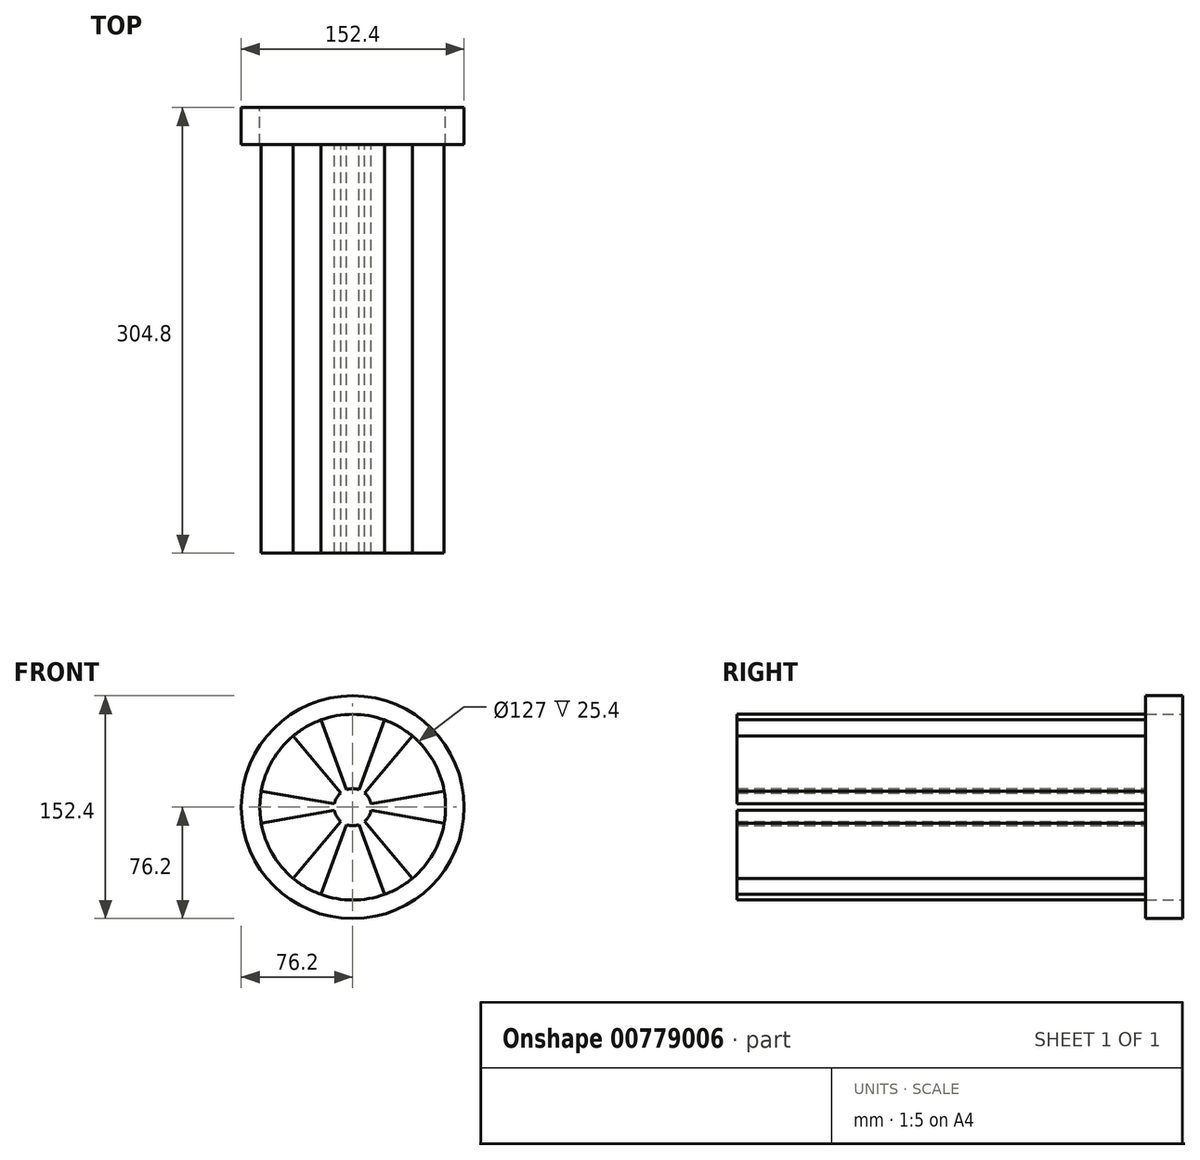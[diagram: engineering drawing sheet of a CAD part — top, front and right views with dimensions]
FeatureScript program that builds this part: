
annotation { "Feature Type Name" : "Feature", "Feature Type Description" : "" }
export const myFeature = defineFeature(function(context is Context, id is Id, definition is map)
    precondition{}
    {
        {
            var Q0;
            Q0=qCreatedBy(makeId("Front.planeOp"),FACE);
            var sketch = newSketch(context, id + "F0", { "sketchPlane" : qUnion([Q0])});
            skCircle(sketch, "E0", {"center": v(0, 0) * mm, "radius": 76.2 * mm});
            skCircle(sketch, "E1", {"center": v(0, 0) * mm, "radius": 12.7 * mm});
            skLineSegment(sketch, "E2", {"start": v(0, 12.7) * mm, "end": v(0, 76.2) * mm});
            skLineSegment(sketch, "E3.1.0", {"start": v(-4.34, 11.93) * mm, "end": v(-26.06, 71.6) * mm});
            skLineSegment(sketch, "E3.2.0", {"start": v(-8.16, 9.73) * mm, "end": v(-48.98, 58.37) * mm});
            skLineSegment(sketch, "E3.3.0", {"start": v(-11, 6.35) * mm, "end": v(-66, 38.1) * mm});
            skLineSegment(sketch, "E3.4.0", {"start": v(-12.5, 2.2) * mm, "end": v(-75.04, 13.23) * mm});
            skLineSegment(sketch, "E3.5.0", {"start": v(-12.5, -2.2) * mm, "end": v(-75.04, -13.23) * mm});
            skLineSegment(sketch, "E3.6.0", {"start": v(-11, -6.35) * mm, "end": v(-66, -38.1) * mm});
            skLineSegment(sketch, "E3.7.0", {"start": v(-8.16, -9.73) * mm, "end": v(-48.98, -58.37) * mm});
            skLineSegment(sketch, "E3.8.0", {"start": v(-4.34, -11.93) * mm, "end": v(-26.06, -71.6) * mm});
            skLineSegment(sketch, "E3.9.0", {"start": v(0, -12.7) * mm, "end": v(0, -76.2) * mm});
            skLineSegment(sketch, "E3.10.0", {"start": v(4.34, -11.93) * mm, "end": v(26.06, -71.6) * mm});
            skLineSegment(sketch, "E3.11.0", {"start": v(8.16, -9.73) * mm, "end": v(48.98, -58.37) * mm});
            skLineSegment(sketch, "E3.12.0", {"start": v(11, -6.35) * mm, "end": v(66, -38.1) * mm});
            skLineSegment(sketch, "E3.13.0", {"start": v(12.5, -2.2) * mm, "end": v(75.04, -13.23) * mm});
            skLineSegment(sketch, "E3.14.0", {"start": v(12.5, 2.2) * mm, "end": v(75.04, 13.23) * mm});
            skLineSegment(sketch, "E3.15.0", {"start": v(11, 6.35) * mm, "end": v(66, 38.1) * mm});
            skLineSegment(sketch, "E3.16.0", {"start": v(8.16, 9.73) * mm, "end": v(48.98, 58.37) * mm});
            skLineSegment(sketch, "E3.17.0", {"start": v(4.34, 11.93) * mm, "end": v(26.06, 71.6) * mm});
            skCircle(sketch, "E4", {"center": v(0, 0) * mm, "radius": 63.5 * mm});
            skSolve(sketch);
        }
        {
            var Q0;
            {var subQ0=sQuery(id+"F0.wireOp",EDGE,"E1");var subQ8=makeQuery(id+"F0.imprint","INTERSECT",VERTEX,{"derivedFrom":[subQ0,sQuery(id+"F0.wireOp",EDGE,"E3.14.0")]});Q0=makeQuery(id+"F0.imprint","IMPRINT",FACE,{"disambiguationData":[TD([[makeQuery(id+"F0.imprint","IMPRINT",EDGE,{"disambiguationData":[TD([[subQ8,-1.0]])],"derivedFrom":subQ0}),1.0]])]});}
            var Q1;
            {var subQ0=sQuery(id+"F0.wireOp",EDGE,"E3.5.0");var subQ1=sQuery(id+"F0.wireOp",EDGE,"E1");var subQ2=makeQuery(id+"F0.imprint","INTERSECT",VERTEX,{"derivedFrom":[subQ1,subQ0]});Q1=makeQuery(id+"F0.imprint","IMPRINT",FACE,{"disambiguationData":[TD([[makeQuery(id+"F0.imprint","IMPRINT",EDGE,{"disambiguationData":[TD([[subQ2,-1.0]])],"derivedFrom":subQ1}),-1.0]])]});}
            var Q2;
            {var subQ0=sQuery(id+"F0.wireOp",EDGE,"E2");var subQ1=sQuery(id+"F0.wireOp",EDGE,"E1");var subQ2=makeQuery(id+"F0.imprint","INTERSECT",VERTEX,{"derivedFrom":[subQ1,subQ0]});Q2=makeQuery(id+"F0.imprint","IMPRINT",FACE,{"disambiguationData":[TD([[makeQuery(id+"F0.imprint","IMPRINT",EDGE,{"disambiguationData":[TD([[subQ2,1.0]])],"derivedFrom":subQ1}),-1.0]])]});}
            var Q3;
            {var subQ0=sQuery(id+"F0.wireOp",EDGE,"E3.2.0");var subQ1=sQuery(id+"F0.wireOp",EDGE,"E1");var subQ2=makeQuery(id+"F0.imprint","INTERSECT",VERTEX,{"derivedFrom":[subQ1,subQ0]});Q3=makeQuery(id+"F0.imprint","IMPRINT",FACE,{"disambiguationData":[TD([[makeQuery(id+"F0.imprint","IMPRINT",EDGE,{"disambiguationData":[TD([[subQ2,-1.0]])],"derivedFrom":subQ1}),-1.0]])]});}
            var Q4;
            {var subQ0=sQuery(id+"F0.wireOp",EDGE,"E3.11.0");var subQ1=sQuery(id+"F0.wireOp",EDGE,"E1");var subQ2=makeQuery(id+"F0.imprint","INTERSECT",VERTEX,{"derivedFrom":[subQ1,subQ0]});Q4=makeQuery(id+"F0.imprint","IMPRINT",FACE,{"disambiguationData":[TD([[makeQuery(id+"F0.imprint","IMPRINT",EDGE,{"disambiguationData":[TD([[subQ2,-1.0]])],"derivedFrom":subQ1}),-1.0]])]});}
            var Q5;
            {var subQ0=sQuery(id+"F0.wireOp",EDGE,"E3.14.0");var subQ1=sQuery(id+"F0.wireOp",EDGE,"E1");var subQ2=makeQuery(id+"F0.imprint","INTERSECT",VERTEX,{"derivedFrom":[subQ1,subQ0]});Q5=makeQuery(id+"F0.imprint","IMPRINT",FACE,{"disambiguationData":[TD([[makeQuery(id+"F0.imprint","IMPRINT",EDGE,{"disambiguationData":[TD([[subQ2,-1.0]])],"derivedFrom":subQ1}),-1.0]])]});}
            var Q6;
            {var subQ0=sQuery(id+"F0.wireOp",EDGE,"E3.8.0");var subQ1=sQuery(id+"F0.wireOp",EDGE,"E1");var subQ2=makeQuery(id+"F0.imprint","INTERSECT",VERTEX,{"derivedFrom":[subQ1,subQ0]});Q6=makeQuery(id+"F0.imprint","IMPRINT",FACE,{"disambiguationData":[TD([[makeQuery(id+"F0.imprint","IMPRINT",EDGE,{"disambiguationData":[TD([[subQ2,-1.0]])],"derivedFrom":subQ1}),-1.0]])]});}
            extrude(context, id + "F1", {"entities" : qUnion([Q0, Q1, Q2, Q3, Q4, Q5, Q6]), "depth" : 25.4 * mm, "offsetDistance" : 25.4 * mm});
        }
        {
            var Q0;
            {var subQ0=sQuery(id+"F0.wireOp",EDGE,"E3.9.0");var subQ1=sQuery(id+"F0.wireOp",EDGE,"E0");var subQ2=makeQuery(id+"F0.imprint","INTERSECT",VERTEX,{"derivedFrom":[subQ1,subQ0]});Q0=makeQuery(id+"F0.imprint","IMPRINT",FACE,{"disambiguationData":[TD([[makeQuery(id+"F0.imprint","IMPRINT",EDGE,{"disambiguationData":[TD([[subQ2,-1.0]])],"derivedFrom":subQ1}),1.0]])]});}
            var Q1;
            {var subQ0=sQuery(id+"F0.wireOp",EDGE,"E3.13.0");var subQ1=sQuery(id+"F0.wireOp",EDGE,"E0");var subQ2=makeQuery(id+"F0.imprint","INTERSECT",VERTEX,{"derivedFrom":[subQ1,subQ0]});Q1=makeQuery(id+"F0.imprint","IMPRINT",FACE,{"disambiguationData":[TD([[makeQuery(id+"F0.imprint","IMPRINT",EDGE,{"disambiguationData":[TD([[subQ2,-1.0]])],"derivedFrom":subQ1}),1.0]])]});}
            var Q2;
            {var subQ0=sQuery(id+"F0.wireOp",EDGE,"E2");var subQ1=sQuery(id+"F0.wireOp",EDGE,"E0");var subQ2=makeQuery(id+"F0.imprint","INTERSECT",VERTEX,{"derivedFrom":[subQ1,subQ0]});Q2=makeQuery(id+"F0.imprint","IMPRINT",FACE,{"disambiguationData":[TD([[makeQuery(id+"F0.imprint","IMPRINT",EDGE,{"disambiguationData":[TD([[subQ2,-1.0]])],"derivedFrom":subQ1}),1.0]])]});}
            var Q3;
            {var subQ0=sQuery(id+"F0.wireOp",EDGE,"E3.3.0");var subQ1=sQuery(id+"F0.wireOp",EDGE,"E0");var subQ2=makeQuery(id+"F0.imprint","INTERSECT",VERTEX,{"derivedFrom":[subQ1,subQ0]});Q3=makeQuery(id+"F0.imprint","IMPRINT",FACE,{"disambiguationData":[TD([[makeQuery(id+"F0.imprint","IMPRINT",EDGE,{"disambiguationData":[TD([[subQ2,-1.0]])],"derivedFrom":subQ1}),1.0]])]});}
            var Q4;
            {var subQ0=sQuery(id+"F0.wireOp",EDGE,"E3.5.0");var subQ1=sQuery(id+"F0.wireOp",EDGE,"E0");var subQ2=makeQuery(id+"F0.imprint","INTERSECT",VERTEX,{"derivedFrom":[subQ1,subQ0]});Q4=makeQuery(id+"F0.imprint","IMPRINT",FACE,{"disambiguationData":[TD([[makeQuery(id+"F0.imprint","IMPRINT",EDGE,{"disambiguationData":[TD([[subQ2,-1.0]])],"derivedFrom":subQ1}),1.0]])]});}
            var Q5;
            {var subQ0=sQuery(id+"F0.wireOp",EDGE,"E3.7.0");var subQ1=sQuery(id+"F0.wireOp",EDGE,"E0");var subQ2=makeQuery(id+"F0.imprint","INTERSECT",VERTEX,{"derivedFrom":[subQ1,subQ0]});Q5=makeQuery(id+"F0.imprint","IMPRINT",FACE,{"disambiguationData":[TD([[makeQuery(id+"F0.imprint","IMPRINT",EDGE,{"disambiguationData":[TD([[subQ2,-1.0]])],"derivedFrom":subQ1}),1.0]])]});}
            var Q6;
            {var subQ0=sQuery(id+"F0.wireOp",EDGE,"E2");var subQ1=sQuery(id+"F0.wireOp",EDGE,"E0");var subQ2=makeQuery(id+"F0.imprint","INTERSECT",VERTEX,{"derivedFrom":[subQ1,subQ0]});Q6=makeQuery(id+"F0.imprint","IMPRINT",FACE,{"disambiguationData":[TD([[makeQuery(id+"F0.imprint","IMPRINT",EDGE,{"disambiguationData":[TD([[subQ2,1.0]])],"derivedFrom":subQ1}),1.0]])]});}
            var Q7;
            {var subQ0=sQuery(id+"F0.wireOp",EDGE,"E3.10.0");var subQ1=sQuery(id+"F0.wireOp",EDGE,"E0");var subQ2=makeQuery(id+"F0.imprint","INTERSECT",VERTEX,{"derivedFrom":[subQ1,subQ0]});Q7=makeQuery(id+"F0.imprint","IMPRINT",FACE,{"disambiguationData":[TD([[makeQuery(id+"F0.imprint","IMPRINT",EDGE,{"disambiguationData":[TD([[subQ2,-1.0]])],"derivedFrom":subQ1}),1.0]])]});}
            var Q8;
            {var subQ0=sQuery(id+"F0.wireOp",EDGE,"E3.14.0");var subQ1=sQuery(id+"F0.wireOp",EDGE,"E0");var subQ2=makeQuery(id+"F0.imprint","INTERSECT",VERTEX,{"derivedFrom":[subQ1,subQ0]});Q8=makeQuery(id+"F0.imprint","IMPRINT",FACE,{"disambiguationData":[TD([[makeQuery(id+"F0.imprint","IMPRINT",EDGE,{"disambiguationData":[TD([[subQ2,-1.0]])],"derivedFrom":subQ1}),1.0]])]});}
            var Q9;
            {var subQ0=sQuery(id+"F0.wireOp",EDGE,"E3.11.0");var subQ1=sQuery(id+"F0.wireOp",EDGE,"E0");var subQ2=makeQuery(id+"F0.imprint","INTERSECT",VERTEX,{"derivedFrom":[subQ1,subQ0]});Q9=makeQuery(id+"F0.imprint","IMPRINT",FACE,{"disambiguationData":[TD([[makeQuery(id+"F0.imprint","IMPRINT",EDGE,{"disambiguationData":[TD([[subQ2,-1.0]])],"derivedFrom":subQ1}),1.0]])]});}
            var Q10;
            {var subQ0=sQuery(id+"F0.wireOp",EDGE,"E3.8.0");var subQ1=sQuery(id+"F0.wireOp",EDGE,"E0");var subQ2=makeQuery(id+"F0.imprint","INTERSECT",VERTEX,{"derivedFrom":[subQ1,subQ0]});Q10=makeQuery(id+"F0.imprint","IMPRINT",FACE,{"disambiguationData":[TD([[makeQuery(id+"F0.imprint","IMPRINT",EDGE,{"disambiguationData":[TD([[subQ2,-1.0]])],"derivedFrom":subQ1}),1.0]])]});}
            var Q11;
            {var subQ0=sQuery(id+"F0.wireOp",EDGE,"E3.15.0");var subQ1=sQuery(id+"F0.wireOp",EDGE,"E0");var subQ2=makeQuery(id+"F0.imprint","INTERSECT",VERTEX,{"derivedFrom":[subQ1,subQ0]});Q11=makeQuery(id+"F0.imprint","IMPRINT",FACE,{"disambiguationData":[TD([[makeQuery(id+"F0.imprint","IMPRINT",EDGE,{"disambiguationData":[TD([[subQ2,-1.0]])],"derivedFrom":subQ1}),1.0]])]});}
            var Q12;
            Q12 = qSketchRegion(id + "F0", true);
            var Q13;
            {var subQ0=sQuery(id+"F0.wireOp",EDGE,"E3.4.0");var subQ1=sQuery(id+"F0.wireOp",EDGE,"E0");var subQ2=makeQuery(id+"F0.imprint","INTERSECT",VERTEX,{"derivedFrom":[subQ1,subQ0]});Q13=makeQuery(id+"F0.imprint","IMPRINT",FACE,{"disambiguationData":[TD([[makeQuery(id+"F0.imprint","IMPRINT",EDGE,{"disambiguationData":[TD([[subQ2,-1.0]])],"derivedFrom":subQ1}),1.0]])]});}
            var Q14;
            {var subQ0=sQuery(id+"F0.wireOp",EDGE,"E3.12.0");var subQ1=sQuery(id+"F0.wireOp",EDGE,"E0");var subQ2=makeQuery(id+"F0.imprint","INTERSECT",VERTEX,{"derivedFrom":[subQ1,subQ0]});Q14=makeQuery(id+"F0.imprint","IMPRINT",FACE,{"disambiguationData":[TD([[makeQuery(id+"F0.imprint","IMPRINT",EDGE,{"disambiguationData":[TD([[subQ2,-1.0]])],"derivedFrom":subQ1}),1.0]])]});}
            var Q15;
            {var subQ0=sQuery(id+"F0.wireOp",EDGE,"E3.2.0");var subQ1=sQuery(id+"F0.wireOp",EDGE,"E0");var subQ2=makeQuery(id+"F0.imprint","INTERSECT",VERTEX,{"derivedFrom":[subQ1,subQ0]});Q15=makeQuery(id+"F0.imprint","IMPRINT",FACE,{"disambiguationData":[TD([[makeQuery(id+"F0.imprint","IMPRINT",EDGE,{"disambiguationData":[TD([[subQ2,-1.0]])],"derivedFrom":subQ1}),1.0]])]});}
            var Q16;
            {var subQ0=sQuery(id+"F0.wireOp",EDGE,"E3.16.0");var subQ1=sQuery(id+"F0.wireOp",EDGE,"E0");var subQ2=makeQuery(id+"F0.imprint","INTERSECT",VERTEX,{"derivedFrom":[subQ1,subQ0]});Q16=makeQuery(id+"F0.imprint","IMPRINT",FACE,{"disambiguationData":[TD([[makeQuery(id+"F0.imprint","IMPRINT",EDGE,{"disambiguationData":[TD([[subQ2,-1.0]])],"derivedFrom":subQ1}),1.0]])]});}
            var Q17;
            {var subQ0=sQuery(id+"F0.wireOp",EDGE,"E3.1.0");var subQ1=sQuery(id+"F0.wireOp",EDGE,"E0");var subQ2=makeQuery(id+"F0.imprint","INTERSECT",VERTEX,{"derivedFrom":[subQ1,subQ0]});Q17=makeQuery(id+"F0.imprint","IMPRINT",FACE,{"disambiguationData":[TD([[makeQuery(id+"F0.imprint","IMPRINT",EDGE,{"disambiguationData":[TD([[subQ2,-1.0]])],"derivedFrom":subQ1}),1.0]])]});}
            var Q18;
            {var subQ0=sQuery(id+"F0.wireOp",EDGE,"E3.6.0");var subQ1=sQuery(id+"F0.wireOp",EDGE,"E0");var subQ2=makeQuery(id+"F0.imprint","INTERSECT",VERTEX,{"derivedFrom":[subQ1,subQ0]});Q18=makeQuery(id+"F0.imprint","IMPRINT",FACE,{"disambiguationData":[TD([[makeQuery(id+"F0.imprint","IMPRINT",EDGE,{"disambiguationData":[TD([[subQ2,-1.0]])],"derivedFrom":subQ1}),1.0]])]});}
            var Q19;
            {var subQ0=sQuery(id+"F0.wireOp",EDGE,"E3.1.0");var subQ1=sQuery(id+"F0.wireOp",EDGE,"E1");var subQ2=makeQuery(id+"F0.imprint","INTERSECT",VERTEX,{"derivedFrom":[subQ1,subQ0]});Q19=makeQuery(id+"F0.imprint","IMPRINT",FACE,{"disambiguationData":[TD([[makeQuery(id+"F0.imprint","IMPRINT",EDGE,{"disambiguationData":[TD([[subQ2,-1.0]])],"derivedFrom":subQ1}),-1.0]])]});}
            var Q20;
            {var subQ0=sQuery(id+"F0.wireOp",EDGE,"E3.16.0");var subQ1=sQuery(id+"F0.wireOp",EDGE,"E1");var subQ2=makeQuery(id+"F0.imprint","INTERSECT",VERTEX,{"derivedFrom":[subQ1,subQ0]});Q20=makeQuery(id+"F0.imprint","IMPRINT",FACE,{"disambiguationData":[TD([[makeQuery(id+"F0.imprint","IMPRINT",EDGE,{"disambiguationData":[TD([[subQ2,-1.0]])],"derivedFrom":subQ1}),-1.0]])]});}
            var Q21;
            {var subQ0=sQuery(id+"F0.wireOp",EDGE,"E3.13.0");var subQ1=sQuery(id+"F0.wireOp",EDGE,"E1");var subQ2=makeQuery(id+"F0.imprint","INTERSECT",VERTEX,{"derivedFrom":[subQ1,subQ0]});Q21=makeQuery(id+"F0.imprint","IMPRINT",FACE,{"disambiguationData":[TD([[makeQuery(id+"F0.imprint","IMPRINT",EDGE,{"disambiguationData":[TD([[subQ2,-1.0]])],"derivedFrom":subQ1}),-1.0]])]});}
            var Q22;
            {var subQ0=sQuery(id+"F0.wireOp",EDGE,"E3.10.0");var subQ1=sQuery(id+"F0.wireOp",EDGE,"E1");var subQ2=makeQuery(id+"F0.imprint","INTERSECT",VERTEX,{"derivedFrom":[subQ1,subQ0]});Q22=makeQuery(id+"F0.imprint","IMPRINT",FACE,{"disambiguationData":[TD([[makeQuery(id+"F0.imprint","IMPRINT",EDGE,{"disambiguationData":[TD([[subQ2,-1.0]])],"derivedFrom":subQ1}),-1.0]])]});}
            var Q23;
            {var subQ0=sQuery(id+"F0.wireOp",EDGE,"E3.7.0");var subQ1=sQuery(id+"F0.wireOp",EDGE,"E1");var subQ2=makeQuery(id+"F0.imprint","INTERSECT",VERTEX,{"derivedFrom":[subQ1,subQ0]});Q23=makeQuery(id+"F0.imprint","IMPRINT",FACE,{"disambiguationData":[TD([[makeQuery(id+"F0.imprint","IMPRINT",EDGE,{"disambiguationData":[TD([[subQ2,-1.0]])],"derivedFrom":subQ1}),-1.0]])]});}
            var Q24;
            {var subQ0=sQuery(id+"F0.wireOp",EDGE,"E3.4.0");var subQ1=sQuery(id+"F0.wireOp",EDGE,"E1");var subQ2=makeQuery(id+"F0.imprint","INTERSECT",VERTEX,{"derivedFrom":[subQ1,subQ0]});Q24=makeQuery(id+"F0.imprint","IMPRINT",FACE,{"disambiguationData":[TD([[makeQuery(id+"F0.imprint","IMPRINT",EDGE,{"disambiguationData":[TD([[subQ2,-1.0]])],"derivedFrom":subQ1}),-1.0]])]});}
            var Q25;
            {var subQ0=sQuery(id+"F0.wireOp",EDGE,"E3.11.0");var subQ1=sQuery(id+"F0.wireOp",EDGE,"E1");var subQ2=makeQuery(id+"F0.imprint","INTERSECT",VERTEX,{"derivedFrom":[subQ1,subQ0]});Q25=makeQuery(id+"F0.imprint","IMPRINT",FACE,{"disambiguationData":[TD([[makeQuery(id+"F0.imprint","IMPRINT",EDGE,{"disambiguationData":[TD([[subQ2,-1.0]])],"derivedFrom":subQ1}),-1.0]])]});}
            var Q26;
            {var subQ0=sQuery(id+"F0.wireOp",EDGE,"E3.14.0");var subQ1=sQuery(id+"F0.wireOp",EDGE,"E1");var subQ2=makeQuery(id+"F0.imprint","INTERSECT",VERTEX,{"derivedFrom":[subQ1,subQ0]});Q26=makeQuery(id+"F0.imprint","IMPRINT",FACE,{"disambiguationData":[TD([[makeQuery(id+"F0.imprint","IMPRINT",EDGE,{"disambiguationData":[TD([[subQ2,-1.0]])],"derivedFrom":subQ1}),-1.0]])]});}
            var Q27;
            {var subQ0=sQuery(id+"F0.wireOp",EDGE,"E2");var subQ1=sQuery(id+"F0.wireOp",EDGE,"E1");var subQ2=makeQuery(id+"F0.imprint","INTERSECT",VERTEX,{"derivedFrom":[subQ1,subQ0]});Q27=makeQuery(id+"F0.imprint","IMPRINT",FACE,{"disambiguationData":[TD([[makeQuery(id+"F0.imprint","IMPRINT",EDGE,{"disambiguationData":[TD([[subQ2,1.0]])],"derivedFrom":subQ1}),-1.0]])]});}
            var Q28;
            {var subQ0=sQuery(id+"F0.wireOp",EDGE,"E3.8.0");var subQ1=sQuery(id+"F0.wireOp",EDGE,"E1");var subQ2=makeQuery(id+"F0.imprint","INTERSECT",VERTEX,{"derivedFrom":[subQ1,subQ0]});Q28=makeQuery(id+"F0.imprint","IMPRINT",FACE,{"disambiguationData":[TD([[makeQuery(id+"F0.imprint","IMPRINT",EDGE,{"disambiguationData":[TD([[subQ2,-1.0]])],"derivedFrom":subQ1}),-1.0]])]});}
            var Q29;
            {var subQ0=sQuery(id+"F0.wireOp",EDGE,"E3.2.0");var subQ1=sQuery(id+"F0.wireOp",EDGE,"E1");var subQ2=makeQuery(id+"F0.imprint","INTERSECT",VERTEX,{"derivedFrom":[subQ1,subQ0]});Q29=makeQuery(id+"F0.imprint","IMPRINT",FACE,{"disambiguationData":[TD([[makeQuery(id+"F0.imprint","IMPRINT",EDGE,{"disambiguationData":[TD([[subQ2,-1.0]])],"derivedFrom":subQ1}),-1.0]])]});}
            var Q30;
            {var subQ0=sQuery(id+"F0.wireOp",EDGE,"E3.5.0");var subQ1=sQuery(id+"F0.wireOp",EDGE,"E1");var subQ2=makeQuery(id+"F0.imprint","INTERSECT",VERTEX,{"derivedFrom":[subQ1,subQ0]});Q30=makeQuery(id+"F0.imprint","IMPRINT",FACE,{"disambiguationData":[TD([[makeQuery(id+"F0.imprint","IMPRINT",EDGE,{"disambiguationData":[TD([[subQ2,-1.0]])],"derivedFrom":subQ1}),-1.0]])]});}
            extrude(context, id + "F2", {"entities" : qUnion([Q0, Q1, Q2, Q3, Q4, Q5, Q6, Q7, Q8, Q9, Q10, Q11, Q12, Q13, Q14, Q15, Q16, Q17, Q18, Q19, Q20, Q21, Q22, Q23, Q24, Q25, Q26, Q27, Q28, Q29, Q30]), "depth" : 25.4 * mm, "offsetDistance" : 25.4 * mm});
        }
        {
            var Q0;
            {var subQ0=sQuery(id+"F0.wireOp",EDGE,"E3.15.0");var subQ1=sQuery(id+"F0.wireOp",EDGE,"E1");var subQ2=makeQuery(id+"F0.imprint","INTERSECT",VERTEX,{"derivedFrom":[subQ1,subQ0]});Q0=makeQuery(id+"F0.imprint","IMPRINT",FACE,{"disambiguationData":[TD([[makeQuery(id+"F0.imprint","IMPRINT",EDGE,{"disambiguationData":[TD([[subQ2,-1.0]])],"derivedFrom":subQ1}),-1.0]])]});}
            var Q1;
            {var subQ0=sQuery(id+"F0.wireOp",EDGE,"E1");var subQ8=makeQuery(id+"F0.imprint","INTERSECT",VERTEX,{"derivedFrom":[subQ0,sQuery(id+"F0.wireOp",EDGE,"E3.14.0")]});Q1=makeQuery(id+"F0.imprint","IMPRINT",FACE,{"disambiguationData":[TD([[makeQuery(id+"F0.imprint","IMPRINT",EDGE,{"disambiguationData":[TD([[subQ8,-1.0]])],"derivedFrom":subQ0}),1.0]])]});}
            var Q2;
            {var subQ0=sQuery(id+"F0.wireOp",EDGE,"E2");var subQ1=sQuery(id+"F0.wireOp",EDGE,"E1");var subQ2=makeQuery(id+"F0.imprint","INTERSECT",VERTEX,{"derivedFrom":[subQ1,subQ0]});Q2=makeQuery(id+"F0.imprint","IMPRINT",FACE,{"disambiguationData":[TD([[makeQuery(id+"F0.imprint","IMPRINT",EDGE,{"disambiguationData":[TD([[subQ2,-1.0]])],"derivedFrom":subQ1}),-1.0]])]});}
            var Q3;
            {var subQ0=sQuery(id+"F0.wireOp",EDGE,"E3.3.0");var subQ1=sQuery(id+"F0.wireOp",EDGE,"E1");var subQ2=makeQuery(id+"F0.imprint","INTERSECT",VERTEX,{"derivedFrom":[subQ1,subQ0]});Q3=makeQuery(id+"F0.imprint","IMPRINT",FACE,{"disambiguationData":[TD([[makeQuery(id+"F0.imprint","IMPRINT",EDGE,{"disambiguationData":[TD([[subQ2,-1.0]])],"derivedFrom":subQ1}),-1.0]])]});}
            var Q4;
            {var subQ0=sQuery(id+"F0.wireOp",EDGE,"E3.12.0");var subQ1=sQuery(id+"F0.wireOp",EDGE,"E1");var subQ2=makeQuery(id+"F0.imprint","INTERSECT",VERTEX,{"derivedFrom":[subQ1,subQ0]});Q4=makeQuery(id+"F0.imprint","IMPRINT",FACE,{"disambiguationData":[TD([[makeQuery(id+"F0.imprint","IMPRINT",EDGE,{"disambiguationData":[TD([[subQ2,-1.0]])],"derivedFrom":subQ1}),-1.0]])]});}
            var Q5;
            {var subQ0=sQuery(id+"F0.wireOp",EDGE,"E3.6.0");var subQ1=sQuery(id+"F0.wireOp",EDGE,"E1");var subQ2=makeQuery(id+"F0.imprint","INTERSECT",VERTEX,{"derivedFrom":[subQ1,subQ0]});Q5=makeQuery(id+"F0.imprint","IMPRINT",FACE,{"disambiguationData":[TD([[makeQuery(id+"F0.imprint","IMPRINT",EDGE,{"disambiguationData":[TD([[subQ2,-1.0]])],"derivedFrom":subQ1}),-1.0]])]});}
            var Q6;
            {var subQ0=sQuery(id+"F0.wireOp",EDGE,"E3.9.0");var subQ1=sQuery(id+"F0.wireOp",EDGE,"E1");var subQ2=makeQuery(id+"F0.imprint","INTERSECT",VERTEX,{"derivedFrom":[subQ1,subQ0]});Q6=makeQuery(id+"F0.imprint","IMPRINT",FACE,{"disambiguationData":[TD([[makeQuery(id+"F0.imprint","IMPRINT",EDGE,{"disambiguationData":[TD([[subQ2,-1.0]])],"derivedFrom":subQ1}),-1.0]])]});}
            extrude(context, id + "F3", {"entities" : qUnion([Q0, Q1, Q2, Q3, Q4, Q5, Q6]), "depth" : 25.4 * mm, "offsetDistance" : 25.4 * mm});
        }
        {
            var Q0;
            {var subQ0=sQuery(id+"F0.wireOp",EDGE,"E3.5.0");var subQ1=sQuery(id+"F0.wireOp",EDGE,"E1");var subQ2=makeQuery(id+"F0.imprint","INTERSECT",VERTEX,{"derivedFrom":[subQ1,subQ0]});Q0=makeQuery(id+"F0.imprint","IMPRINT",FACE,{"disambiguationData":[TD([[makeQuery(id+"F0.imprint","IMPRINT",EDGE,{"disambiguationData":[TD([[subQ2,-1.0]])],"derivedFrom":subQ1}),-1.0]])]});}
            var Q1;
            {var subQ0=sQuery(id+"F0.wireOp",EDGE,"E3.11.0");var subQ1=sQuery(id+"F0.wireOp",EDGE,"E1");var subQ2=makeQuery(id+"F0.imprint","INTERSECT",VERTEX,{"derivedFrom":[subQ1,subQ0]});Q1=makeQuery(id+"F0.imprint","IMPRINT",FACE,{"disambiguationData":[TD([[makeQuery(id+"F0.imprint","IMPRINT",EDGE,{"disambiguationData":[TD([[subQ2,-1.0]])],"derivedFrom":subQ1}),-1.0]])]});}
            var Q2;
            {var subQ0=sQuery(id+"F0.wireOp",EDGE,"E3.2.0");var subQ1=sQuery(id+"F0.wireOp",EDGE,"E1");var subQ2=makeQuery(id+"F0.imprint","INTERSECT",VERTEX,{"derivedFrom":[subQ1,subQ0]});Q2=makeQuery(id+"F0.imprint","IMPRINT",FACE,{"disambiguationData":[TD([[makeQuery(id+"F0.imprint","IMPRINT",EDGE,{"disambiguationData":[TD([[subQ2,-1.0]])],"derivedFrom":subQ1}),-1.0]])]});}
            var Q3;
            {var subQ0=sQuery(id+"F0.wireOp",EDGE,"E3.8.0");var subQ1=sQuery(id+"F0.wireOp",EDGE,"E1");var subQ2=makeQuery(id+"F0.imprint","INTERSECT",VERTEX,{"derivedFrom":[subQ1,subQ0]});Q3=makeQuery(id+"F0.imprint","IMPRINT",FACE,{"disambiguationData":[TD([[makeQuery(id+"F0.imprint","IMPRINT",EDGE,{"disambiguationData":[TD([[subQ2,-1.0]])],"derivedFrom":subQ1}),-1.0]])]});}
            var Q4;
            {var subQ0=sQuery(id+"F0.wireOp",EDGE,"E3.14.0");var subQ1=sQuery(id+"F0.wireOp",EDGE,"E1");var subQ2=makeQuery(id+"F0.imprint","INTERSECT",VERTEX,{"derivedFrom":[subQ1,subQ0]});Q4=makeQuery(id+"F0.imprint","IMPRINT",FACE,{"disambiguationData":[TD([[makeQuery(id+"F0.imprint","IMPRINT",EDGE,{"disambiguationData":[TD([[subQ2,-1.0]])],"derivedFrom":subQ1}),-1.0]])]});}
            var Q5;
            {var subQ0=sQuery(id+"F0.wireOp",EDGE,"E2");var subQ1=sQuery(id+"F0.wireOp",EDGE,"E1");var subQ2=makeQuery(id+"F0.imprint","INTERSECT",VERTEX,{"derivedFrom":[subQ1,subQ0]});Q5=makeQuery(id+"F0.imprint","IMPRINT",FACE,{"disambiguationData":[TD([[makeQuery(id+"F0.imprint","IMPRINT",EDGE,{"disambiguationData":[TD([[subQ2,1.0]])],"derivedFrom":subQ1}),-1.0]])]});}
            extrude(context, id + "F4", {"entities" : qUnion([Q0, Q1, Q2, Q3, Q4, Q5]), "operationType" : NewBodyOperationType.ADD, "depth" : 304.8 * mm, "offsetDistance" : 25.4 * mm});
        }
        {
            var Q0;
            {var subQ0=sQuery(id+"F0.wireOp",EDGE,"E3.6.0");var subQ1=sQuery(id+"F0.wireOp",EDGE,"E1");var subQ2=makeQuery(id+"F0.imprint","INTERSECT",VERTEX,{"derivedFrom":[subQ1,subQ0]});Q0=makeQuery(id+"F0.imprint","IMPRINT",FACE,{"disambiguationData":[TD([[makeQuery(id+"F0.imprint","IMPRINT",EDGE,{"disambiguationData":[TD([[subQ2,-1.0]])],"derivedFrom":subQ1}),-1.0]])]});}
            var Q1;
            {var subQ0=sQuery(id+"F0.wireOp",EDGE,"E3.9.0");var subQ1=sQuery(id+"F0.wireOp",EDGE,"E1");var subQ2=makeQuery(id+"F0.imprint","INTERSECT",VERTEX,{"derivedFrom":[subQ1,subQ0]});Q1=makeQuery(id+"F0.imprint","IMPRINT",FACE,{"disambiguationData":[TD([[makeQuery(id+"F0.imprint","IMPRINT",EDGE,{"disambiguationData":[TD([[subQ2,-1.0]])],"derivedFrom":subQ1}),-1.0]])]});}
            var Q2;
            {var subQ0=sQuery(id+"F0.wireOp",EDGE,"E3.3.0");var subQ1=sQuery(id+"F0.wireOp",EDGE,"E1");var subQ2=makeQuery(id+"F0.imprint","INTERSECT",VERTEX,{"derivedFrom":[subQ1,subQ0]});Q2=makeQuery(id+"F0.imprint","IMPRINT",FACE,{"disambiguationData":[TD([[makeQuery(id+"F0.imprint","IMPRINT",EDGE,{"disambiguationData":[TD([[subQ2,-1.0]])],"derivedFrom":subQ1}),-1.0]])]});}
            var Q3;
            {var subQ0=sQuery(id+"F0.wireOp",EDGE,"E3.12.0");var subQ1=sQuery(id+"F0.wireOp",EDGE,"E1");var subQ2=makeQuery(id+"F0.imprint","INTERSECT",VERTEX,{"derivedFrom":[subQ1,subQ0]});Q3=makeQuery(id+"F0.imprint","IMPRINT",FACE,{"disambiguationData":[TD([[makeQuery(id+"F0.imprint","IMPRINT",EDGE,{"disambiguationData":[TD([[subQ2,-1.0]])],"derivedFrom":subQ1}),-1.0]])]});}
            var Q4;
            {var subQ0=sQuery(id+"F0.wireOp",EDGE,"E2");var subQ1=sQuery(id+"F0.wireOp",EDGE,"E1");var subQ2=makeQuery(id+"F0.imprint","INTERSECT",VERTEX,{"derivedFrom":[subQ1,subQ0]});Q4=makeQuery(id+"F0.imprint","IMPRINT",FACE,{"disambiguationData":[TD([[makeQuery(id+"F0.imprint","IMPRINT",EDGE,{"disambiguationData":[TD([[subQ2,-1.0]])],"derivedFrom":subQ1}),-1.0]])]});}
            var Q5;
            {var subQ0=sQuery(id+"F0.wireOp",EDGE,"E3.15.0");var subQ1=sQuery(id+"F0.wireOp",EDGE,"E1");var subQ2=makeQuery(id+"F0.imprint","INTERSECT",VERTEX,{"derivedFrom":[subQ1,subQ0]});Q5=makeQuery(id+"F0.imprint","IMPRINT",FACE,{"disambiguationData":[TD([[makeQuery(id+"F0.imprint","IMPRINT",EDGE,{"disambiguationData":[TD([[subQ2,-1.0]])],"derivedFrom":subQ1}),-1.0]])]});}
            extrude(context, id + "F5", {"entities" : qUnion([Q0, Q1, Q2, Q3, Q4, Q5]), "operationType" : NewBodyOperationType.ADD, "depth" : 304.8 * mm, "offsetDistance" : 25.4 * mm});
        }
        {
            var Q0;
            {var subQ0=sQuery(id+"F0.wireOp",EDGE,"E3.16.0");var subQ1=sQuery(id+"F0.wireOp",EDGE,"E0");var subQ2=makeQuery(id+"F0.imprint","INTERSECT",VERTEX,{"derivedFrom":[subQ1,subQ0]});Q0=makeQuery(id+"F0.imprint","IMPRINT",FACE,{"disambiguationData":[TD([[makeQuery(id+"F0.imprint","IMPRINT",EDGE,{"disambiguationData":[TD([[subQ2,-1.0]])],"derivedFrom":subQ1}),1.0]])]});}
            var Q1;
            {var subQ0=sQuery(id+"F0.wireOp",EDGE,"E3.11.0");var subQ1=sQuery(id+"F0.wireOp",EDGE,"E0");var subQ2=makeQuery(id+"F0.imprint","INTERSECT",VERTEX,{"derivedFrom":[subQ1,subQ0]});Q1=makeQuery(id+"F0.imprint","IMPRINT",FACE,{"disambiguationData":[TD([[makeQuery(id+"F0.imprint","IMPRINT",EDGE,{"disambiguationData":[TD([[subQ2,-1.0]])],"derivedFrom":subQ1}),1.0]])]});}
            var Q2;
            {var subQ0=sQuery(id+"F0.wireOp",EDGE,"E3.10.0");var subQ1=sQuery(id+"F0.wireOp",EDGE,"E0");var subQ2=makeQuery(id+"F0.imprint","INTERSECT",VERTEX,{"derivedFrom":[subQ1,subQ0]});Q2=makeQuery(id+"F0.imprint","IMPRINT",FACE,{"disambiguationData":[TD([[makeQuery(id+"F0.imprint","IMPRINT",EDGE,{"disambiguationData":[TD([[subQ2,-1.0]])],"derivedFrom":subQ1}),1.0]])]});}
            var Q3;
            {var subQ0=sQuery(id+"F0.wireOp",EDGE,"E3.1.0");var subQ1=sQuery(id+"F0.wireOp",EDGE,"E0");var subQ2=makeQuery(id+"F0.imprint","INTERSECT",VERTEX,{"derivedFrom":[subQ1,subQ0]});Q3=makeQuery(id+"F0.imprint","IMPRINT",FACE,{"disambiguationData":[TD([[makeQuery(id+"F0.imprint","IMPRINT",EDGE,{"disambiguationData":[TD([[subQ2,-1.0]])],"derivedFrom":subQ1}),1.0]])]});}
            var Q4;
            {var subQ0=sQuery(id+"F0.wireOp",EDGE,"E2");var subQ1=sQuery(id+"F0.wireOp",EDGE,"E0");var subQ2=makeQuery(id+"F0.imprint","INTERSECT",VERTEX,{"derivedFrom":[subQ1,subQ0]});Q4=makeQuery(id+"F0.imprint","IMPRINT",FACE,{"disambiguationData":[TD([[makeQuery(id+"F0.imprint","IMPRINT",EDGE,{"disambiguationData":[TD([[subQ2,1.0]])],"derivedFrom":subQ1}),1.0]])]});}
            var Q5;
            {var subQ0=sQuery(id+"F0.wireOp",EDGE,"E3.4.0");var subQ1=sQuery(id+"F0.wireOp",EDGE,"E0");var subQ2=makeQuery(id+"F0.imprint","INTERSECT",VERTEX,{"derivedFrom":[subQ1,subQ0]});Q5=makeQuery(id+"F0.imprint","IMPRINT",FACE,{"disambiguationData":[TD([[makeQuery(id+"F0.imprint","IMPRINT",EDGE,{"disambiguationData":[TD([[subQ2,-1.0]])],"derivedFrom":subQ1}),1.0]])]});}
            var Q6;
            {var subQ0=sQuery(id+"F0.wireOp",EDGE,"E3.7.0");var subQ1=sQuery(id+"F0.wireOp",EDGE,"E0");var subQ2=makeQuery(id+"F0.imprint","INTERSECT",VERTEX,{"derivedFrom":[subQ1,subQ0]});Q6=makeQuery(id+"F0.imprint","IMPRINT",FACE,{"disambiguationData":[TD([[makeQuery(id+"F0.imprint","IMPRINT",EDGE,{"disambiguationData":[TD([[subQ2,-1.0]])],"derivedFrom":subQ1}),1.0]])]});}
            var Q7;
            {var subQ0=sQuery(id+"F0.wireOp",EDGE,"E3.13.0");var subQ1=sQuery(id+"F0.wireOp",EDGE,"E0");var subQ2=makeQuery(id+"F0.imprint","INTERSECT",VERTEX,{"derivedFrom":[subQ1,subQ0]});Q7=makeQuery(id+"F0.imprint","IMPRINT",FACE,{"disambiguationData":[TD([[makeQuery(id+"F0.imprint","IMPRINT",EDGE,{"disambiguationData":[TD([[subQ2,-1.0]])],"derivedFrom":subQ1}),1.0]])]});}
            var Q8;
            {var subQ0=sQuery(id+"F0.wireOp",EDGE,"E3.12.0");var subQ1=sQuery(id+"F0.wireOp",EDGE,"E0");var subQ2=makeQuery(id+"F0.imprint","INTERSECT",VERTEX,{"derivedFrom":[subQ1,subQ0]});Q8=makeQuery(id+"F0.imprint","IMPRINT",FACE,{"disambiguationData":[TD([[makeQuery(id+"F0.imprint","IMPRINT",EDGE,{"disambiguationData":[TD([[subQ2,-1.0]])],"derivedFrom":subQ1}),1.0]])]});}
            var Q9;
            {var subQ0=sQuery(id+"F0.wireOp",EDGE,"E3.9.0");var subQ1=sQuery(id+"F0.wireOp",EDGE,"E0");var subQ2=makeQuery(id+"F0.imprint","INTERSECT",VERTEX,{"derivedFrom":[subQ1,subQ0]});Q9=makeQuery(id+"F0.imprint","IMPRINT",FACE,{"disambiguationData":[TD([[makeQuery(id+"F0.imprint","IMPRINT",EDGE,{"disambiguationData":[TD([[subQ2,-1.0]])],"derivedFrom":subQ1}),1.0]])]});}
            var Q10;
            {var subQ0=sQuery(id+"F0.wireOp",EDGE,"E2");var subQ1=sQuery(id+"F0.wireOp",EDGE,"E0");var subQ2=makeQuery(id+"F0.imprint","INTERSECT",VERTEX,{"derivedFrom":[subQ1,subQ0]});Q10=makeQuery(id+"F0.imprint","IMPRINT",FACE,{"disambiguationData":[TD([[makeQuery(id+"F0.imprint","IMPRINT",EDGE,{"disambiguationData":[TD([[subQ2,-1.0]])],"derivedFrom":subQ1}),1.0]])]});}
            var Q11;
            {var subQ0=sQuery(id+"F0.wireOp",EDGE,"E3.2.0");var subQ1=sQuery(id+"F0.wireOp",EDGE,"E0");var subQ2=makeQuery(id+"F0.imprint","INTERSECT",VERTEX,{"derivedFrom":[subQ1,subQ0]});Q11=makeQuery(id+"F0.imprint","IMPRINT",FACE,{"disambiguationData":[TD([[makeQuery(id+"F0.imprint","IMPRINT",EDGE,{"disambiguationData":[TD([[subQ2,-1.0]])],"derivedFrom":subQ1}),1.0]])]});}
            var Q12;
            {var subQ0=sQuery(id+"F0.wireOp",EDGE,"E3.15.0");var subQ1=sQuery(id+"F0.wireOp",EDGE,"E0");var subQ2=makeQuery(id+"F0.imprint","INTERSECT",VERTEX,{"derivedFrom":[subQ1,subQ0]});Q12=makeQuery(id+"F0.imprint","IMPRINT",FACE,{"disambiguationData":[TD([[makeQuery(id+"F0.imprint","IMPRINT",EDGE,{"disambiguationData":[TD([[subQ2,-1.0]])],"derivedFrom":subQ1}),1.0]])]});}
            var Q13;
            {var subQ0=sQuery(id+"F0.wireOp",EDGE,"E3.8.0");var subQ1=sQuery(id+"F0.wireOp",EDGE,"E0");var subQ2=makeQuery(id+"F0.imprint","INTERSECT",VERTEX,{"derivedFrom":[subQ1,subQ0]});Q13=makeQuery(id+"F0.imprint","IMPRINT",FACE,{"disambiguationData":[TD([[makeQuery(id+"F0.imprint","IMPRINT",EDGE,{"disambiguationData":[TD([[subQ2,-1.0]])],"derivedFrom":subQ1}),1.0]])]});}
            var Q14;
            {var subQ0=sQuery(id+"F0.wireOp",EDGE,"E3.5.0");var subQ1=sQuery(id+"F0.wireOp",EDGE,"E0");var subQ2=makeQuery(id+"F0.imprint","INTERSECT",VERTEX,{"derivedFrom":[subQ1,subQ0]});Q14=makeQuery(id+"F0.imprint","IMPRINT",FACE,{"disambiguationData":[TD([[makeQuery(id+"F0.imprint","IMPRINT",EDGE,{"disambiguationData":[TD([[subQ2,-1.0]])],"derivedFrom":subQ1}),1.0]])]});}
            var Q15;
            {var subQ0=sQuery(id+"F0.wireOp",EDGE,"E3.3.0");var subQ1=sQuery(id+"F0.wireOp",EDGE,"E0");var subQ2=makeQuery(id+"F0.imprint","INTERSECT",VERTEX,{"derivedFrom":[subQ1,subQ0]});Q15=makeQuery(id+"F0.imprint","IMPRINT",FACE,{"disambiguationData":[TD([[makeQuery(id+"F0.imprint","IMPRINT",EDGE,{"disambiguationData":[TD([[subQ2,-1.0]])],"derivedFrom":subQ1}),1.0]])]});}
            var Q16;
            {var subQ0=sQuery(id+"F0.wireOp",EDGE,"E3.14.0");var subQ1=sQuery(id+"F0.wireOp",EDGE,"E0");var subQ2=makeQuery(id+"F0.imprint","INTERSECT",VERTEX,{"derivedFrom":[subQ1,subQ0]});Q16=makeQuery(id+"F0.imprint","IMPRINT",FACE,{"disambiguationData":[TD([[makeQuery(id+"F0.imprint","IMPRINT",EDGE,{"disambiguationData":[TD([[subQ2,-1.0]])],"derivedFrom":subQ1}),1.0]])]});}
            var Q17;
            {var subQ0=sQuery(id+"F0.wireOp",EDGE,"E3.6.0");var subQ1=sQuery(id+"F0.wireOp",EDGE,"E0");var subQ2=makeQuery(id+"F0.imprint","INTERSECT",VERTEX,{"derivedFrom":[subQ1,subQ0]});Q17=makeQuery(id+"F0.imprint","IMPRINT",FACE,{"disambiguationData":[TD([[makeQuery(id+"F0.imprint","IMPRINT",EDGE,{"disambiguationData":[TD([[subQ2,-1.0]])],"derivedFrom":subQ1}),1.0]])]});}
            extrude(context, id + "F6", {"entities" : qUnion([Q0, Q1, Q2, Q3, Q4, Q5, Q6, Q7, Q8, Q9, Q10, Q11, Q12, Q13, Q14, Q15, Q16, Q17]), "depth" : 25.4 * mm, "offsetDistance" : 25.4 * mm});
        }
    });
